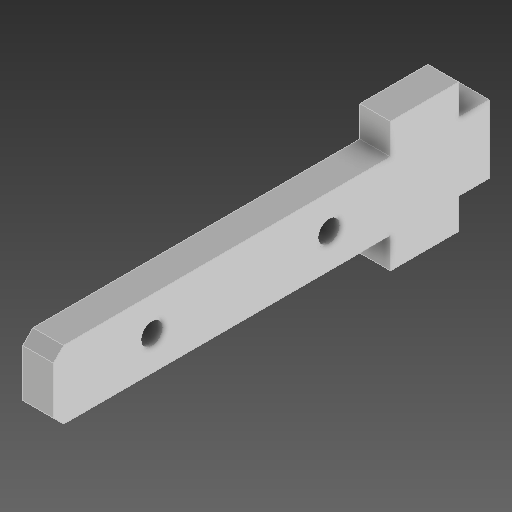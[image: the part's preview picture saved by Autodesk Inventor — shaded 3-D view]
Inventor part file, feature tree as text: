
AUTODESK INVENTOR PART (.ipt)
format: ipt  version: 2020.1 (Build 241239000, 239)  size: 153,088 bytes
history: native  units: mm
features: other x5, sketch x1, extrude x1, hole x1, chamfer x1, projected_geometry x1
ambient origin geometry x8: Origin, YZ Plane, XZ Plane, XY Plane, X Axis, Y Axis, Z Axis, Center Point
bodies: Solid1 (feature_tree)
feature tree (10):
  other  "Inner Rib.ipt"
  sketch  "Sketch the Profile to Extend the Inner Rib Past the Rig Column"  dims[d0=10.0mm d4=10.0mm d5=0.0mm d6=30.0mm d7=54.0mm d8=40.0mm d9=11.0mm d10=6.4mm d11=6.0mm d12=10.0mm d13=5.7mm d14=90.0deg d15=8.0mm d16=20.594885mm d17=3.0mm d18=2.0mm d19=45.0deg d20=0.25mm d21=5.0mm d22=5.0mm]
  extrude  "Extend the Inner Rib Past the Rig Column"  Depth=10.0mm TaperAngle=0.0deg
  hole  "Two Parallel Ribs Get Bolted Together Around the Rig Column"  [1 undecoded]
  chamfer  "Chamfer the Outermost Corners Which Stick Out Away From the Columns"  Distance=54.0mm
  other  "Laser Cut Outer Rib"
  other  "Solid1::Inner Rib.ipt"
  other  "TaggingFeature1"
  other  "Project the Inner Rib Profile"
  projected_geometry  "Projected Loop2"
note: 1 required parameter value undecoded (feature->parameter linkage not recoverable at this tier; creation-order binding heuristic only, values carry confidence <= 0.55)
